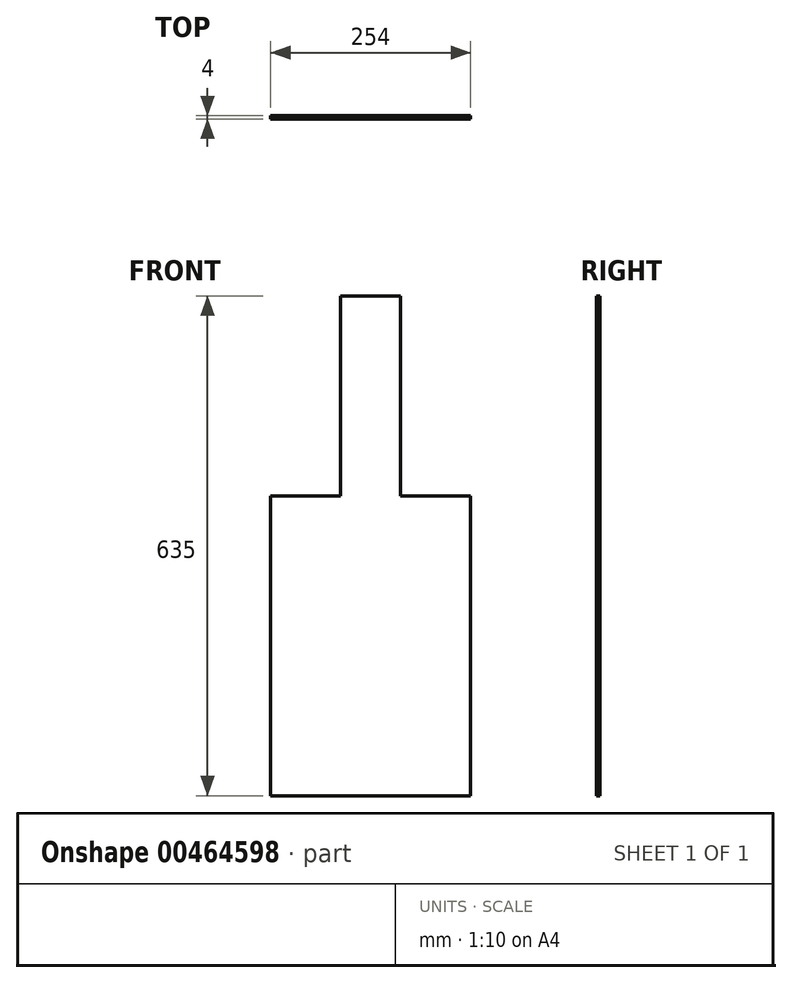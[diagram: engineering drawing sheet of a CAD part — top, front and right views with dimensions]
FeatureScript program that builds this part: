
annotation { "Feature Type Name" : "Feature", "Feature Type Description" : "" }
export const myFeature = defineFeature(function(context is Context, id is Id, definition is map)
    precondition{}
    {
        {
            var Q0;
            Q0=qCreatedBy(makeId("Front.planeOp"),FACE);
            var sketch = newSketch(context, id + "F0", { "sketchPlane" : qUnion([Q0])});
            skLineSegment(sketch, "E0.bottom", {"start": v(127, 190.5) * mm, "end": v(-127, 190.5) * mm, "construction": true});
            skLineSegment(sketch, "E0.top", {"start": v(127, -190.5) * mm, "end": v(-127, -190.5) * mm, "construction": true});
            skLineSegment(sketch, "E0.left", {"start": v(127, 190.5) * mm, "end": v(127, -190.5) * mm, "construction": true});
            skLineSegment(sketch, "E0.right", {"start": v(-127, 190.5) * mm, "end": v(-127, -190.5) * mm, "construction": true});
            skPoint(sketch, "E0.middle", {"position": v(0, 0) * mm});
            skLineSegment(sketch, "E1", {"start": v(-38.1, 190.5) * mm, "end": v(-38.1, 444.5) * mm});
            skLineSegment(sketch, "E2", {"start": v(-38.1, 444.5) * mm, "end": v(38.1, 444.5) * mm});
            skLineSegment(sketch, "E3", {"start": v(38.1, 444.5) * mm, "end": v(38.1, 190.5) * mm});
            skLineSegment(sketch, "E4", {"start": v(38.1, 317.5) * mm, "end": v(-38.1, 317.5) * mm, "construction": true});
            skLineSegment(sketch, "E5", {"start": v(0, 317.5) * mm, "end": v(0, 190.5) * mm, "construction": true});
            skLineSegment(sketch, "E6", {"start": v(-38.1, 190.5) * mm, "end": v(-127, 190.5) * mm});
            skLineSegment(sketch, "E7", {"start": v(-127, 190.5) * mm, "end": v(-127, -190.5) * mm});
            skLineSegment(sketch, "E8", {"start": v(-127, -190.5) * mm, "end": v(127, -190.5) * mm});
            skLineSegment(sketch, "E9", {"start": v(127, -190.5) * mm, "end": v(127, 190.5) * mm});
            skLineSegment(sketch, "E10", {"start": v(127, 190.5) * mm, "end": v(38.1, 190.5) * mm});
            skSolve(sketch);
        }
        {
            var Q0;
            Q0 = qSketchRegion(id + "F0", true);
            extrude(context, id + "F1", {"entities" : qUnion([Q0]), "depth" : 4 * mm});
        }
    });
